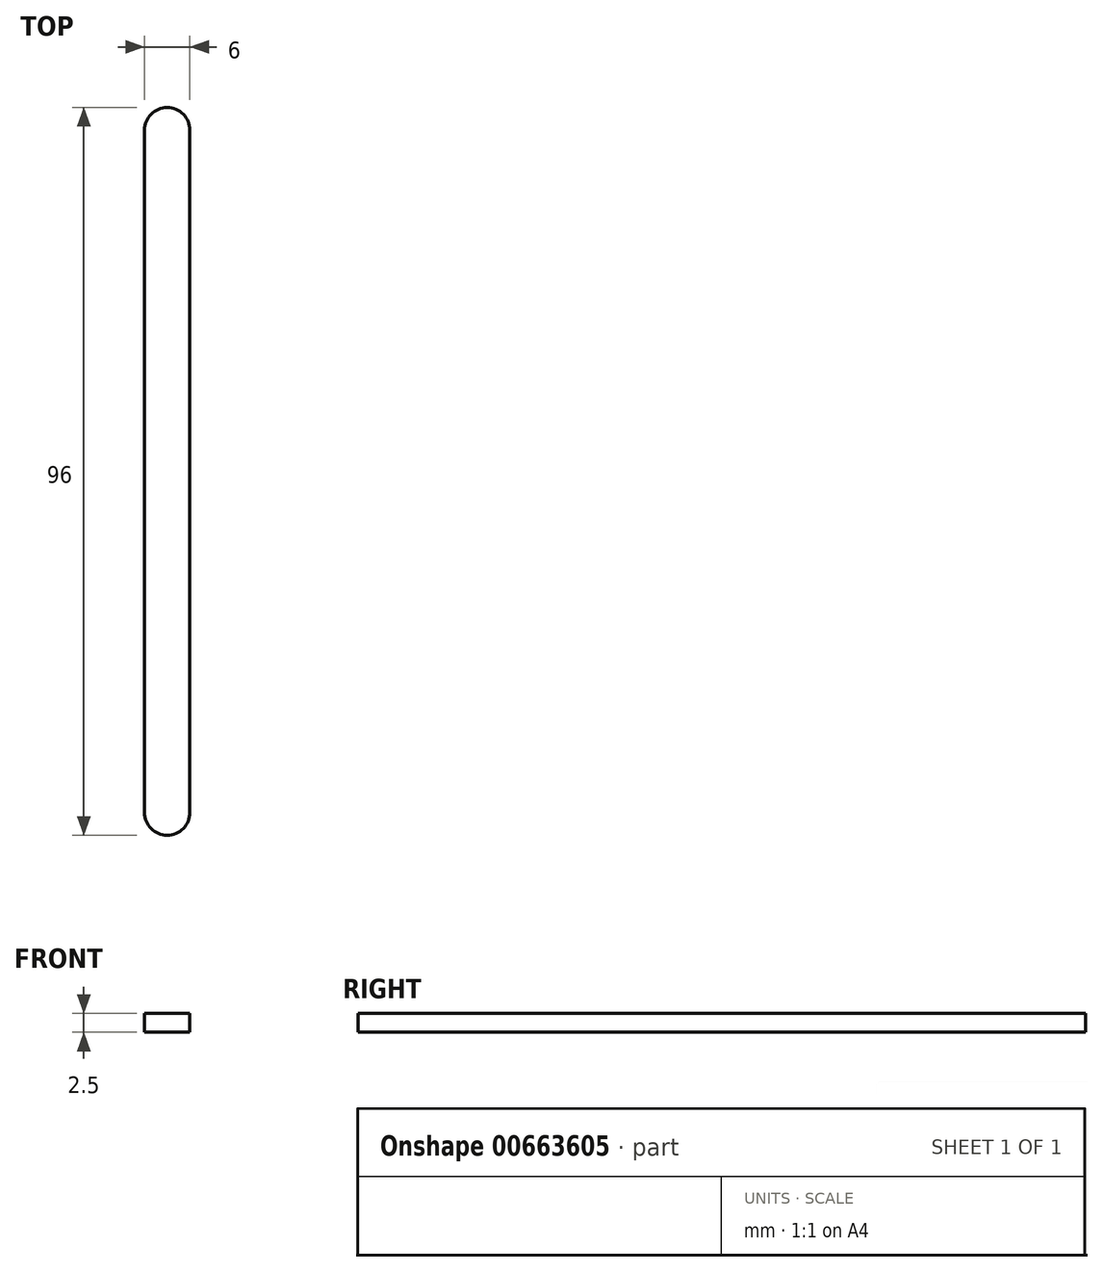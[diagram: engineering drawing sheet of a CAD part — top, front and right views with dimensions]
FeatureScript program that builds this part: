
annotation { "Feature Type Name" : "Feature", "Feature Type Description" : "" }
export const myFeature = defineFeature(function(context is Context, id is Id, definition is map)
    precondition{}
    {
        {
            var Q0;
            Q0=qCreatedBy(makeId("Top.planeOp"),FACE);
            var sketch = newSketch(context, id + "F0", { "sketchPlane" : qUnion([Q0])});
            skLineSegment(sketch, "E0", {"start": v(-3, -45.25) * mm, "end": v(-3, 44.75) * mm});
            skLineSegment(sketch, "E1.MirrorCS", {"start": v(3, -45.25) * mm, "end": v(3, 44.75) * mm});
            skArc(sketch, "E2", {"start": v(-3, 44.75) * mm, "mid": v(0, 47.75) * mm, "end": v(3, 44.75) * mm});
            skArc(sketch, "E3", {"start": v(-3, -45.25) * mm, "mid": v(0, -48.25) * mm, "end": v(3, -45.25) * mm});
            skSolve(sketch);
        }
        {
            var Q0;
            Q0=makeQuery(id+"F0.imprint","IMPRINT",FACE,{"disambiguationData":[TD([[makeQuery(id+"F0.imprint","IMPRINT",EDGE,{"derivedFrom":sQuery(id+"F0.wireOp",EDGE,"E0")}),-1.0]])]});
            extrude(context, id + "F1", {"entities" : qUnion([Q0]), "depth" : 2.5 * mm, "offsetDistance" : 25 * mm});
        }
    });
